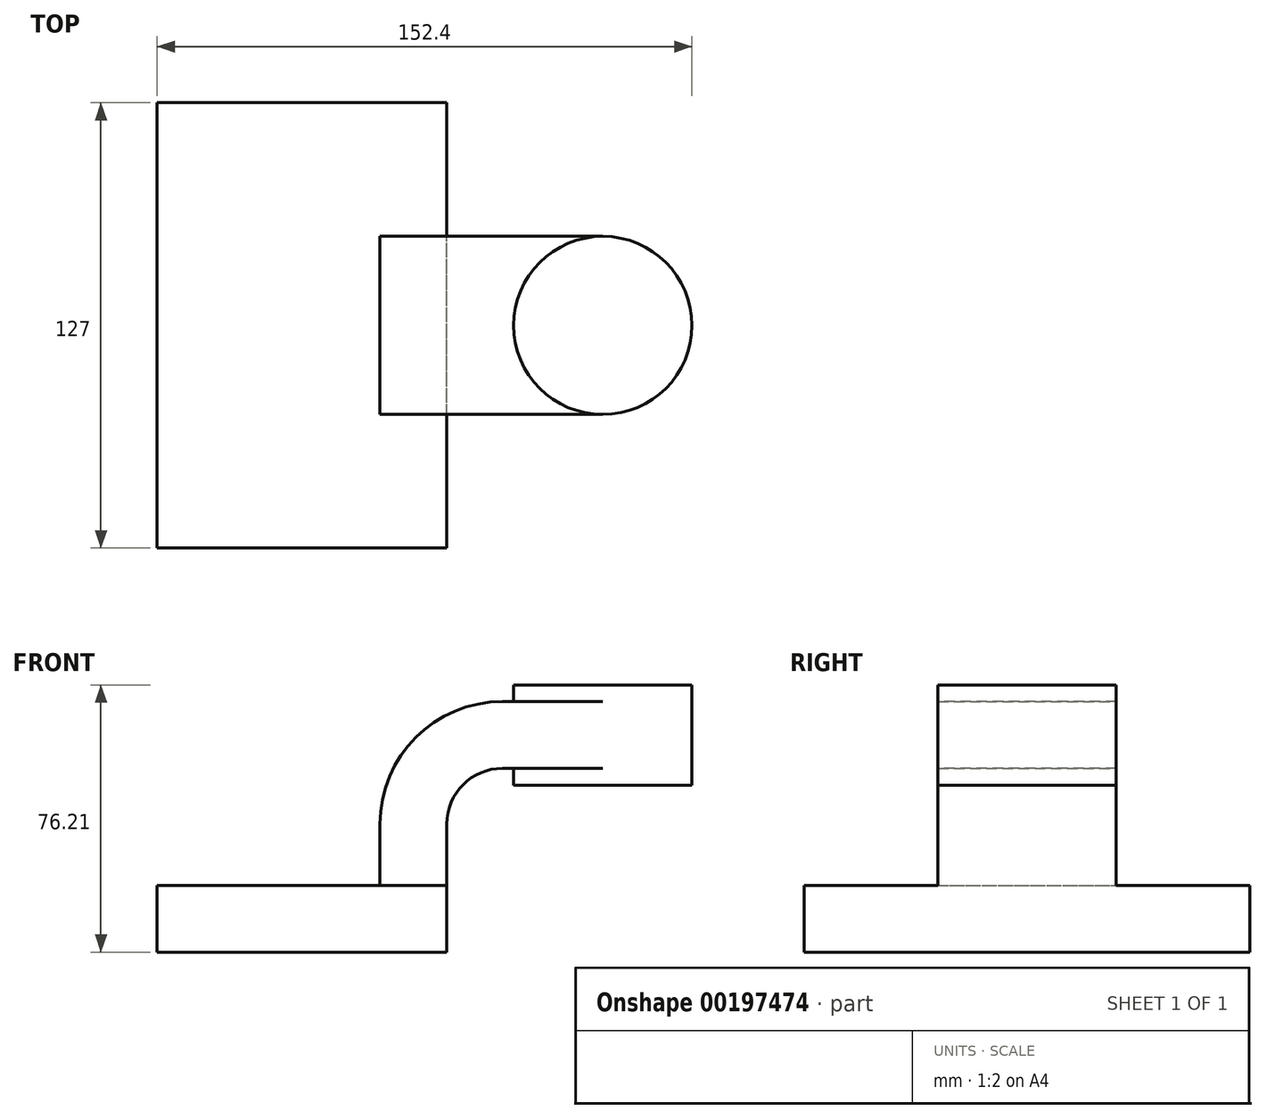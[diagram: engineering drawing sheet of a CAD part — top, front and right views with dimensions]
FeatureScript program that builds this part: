
annotation { "Feature Type Name" : "Feature", "Feature Type Description" : "" }
export const myFeature = defineFeature(function(context is Context, id is Id, definition is map)
    precondition{}
    {
        {
            var Q0;
            Q0=qCreatedBy(makeId("Front.planeOp"),FACE);
            var sketch = newSketch(context, id + "F0", { "sketchPlane" : qUnion([Q0])});
            skLineSegment(sketch, "E0.bottom", {"start": v(-41.27, -9.52) * mm, "end": v(41.28, -9.52) * mm});
            skLineSegment(sketch, "E0.top", {"start": v(-41.28, 9.52) * mm, "end": v(41.27, 9.52) * mm});
            skLineSegment(sketch, "E0.left", {"start": v(-41.27, -9.52) * mm, "end": v(-41.28, 9.52) * mm});
            skLineSegment(sketch, "E0.right", {"start": v(41.28, -9.52) * mm, "end": v(41.27, 9.52) * mm});
            skPoint(sketch, "E0.middle", {"position": v(0, 0) * mm});
            skLineSegment(sketch, "E1.bottom", {"start": v(60.33, 38.1) * mm, "end": v(111.12, 38.1) * mm});
            skLineSegment(sketch, "E1.top", {"start": v(60.32, 66.68) * mm, "end": v(111.12, 66.68) * mm});
            skLineSegment(sketch, "E1.left", {"start": v(60.33, 38.1) * mm, "end": v(60.32, 66.68) * mm});
            skLineSegment(sketch, "E1.right", {"start": v(111.12, 38.1) * mm, "end": v(111.12, 66.68) * mm});
            skPoint(sketch, "E1.middle", {"position": v(85.72, 52.39) * mm});
            skLineSegment(sketch, "E2", {"start": v(41.27, 9.52) * mm, "end": v(41.27, 27) * mm});
            skArc(sketch, "E3", {"start": v(41.27, 27) * mm, "mid": v(45.92, 38.23) * mm, "end": v(57.15, 42.88) * mm});
            skLineSegment(sketch, "E4", {"start": v(57.15, 42.88) * mm, "end": v(85.72, 42.88) * mm});
            skLineSegment(sketch, "E5.0", {"start": v(57.15, 61.93) * mm, "end": v(85.72, 61.93) * mm});
            skArc(sketch, "E5.1", {"start": v(22.23, 27) * mm, "mid": v(32.45, 51.7) * mm, "end": v(57.15, 61.93) * mm});
            skLineSegment(sketch, "E5.2", {"start": v(22.22, 9.52) * mm, "end": v(22.22, 27) * mm});
            skFitSpline(sketch, "E6", {"points": [v(-41.28, 9.53) * mm, v(57.15, 61.93) * mm], "startDerivative": vector(2.22, 88.45) * mm, "endDerivative": vector(124.25, 0) * mm});
            skPoint(sketch, "E7", {"position": v(85.72, 66.68) * mm});
            skLineSegment(sketch, "E8", {"start": v(85.72, 66.68) * mm, "end": v(85.72, 38.1) * mm});
            skSolve(sketch);
        }
        {
            var Q0;
            Q0=makeQuery(id+"F0.imprint","IMPRINT",FACE,{"disambiguationData":[TD([[makeQuery(id+"F0.imprint","IMPRINT",EDGE,{"derivedFrom":sQuery(id+"F0.wireOp",EDGE,"E0.bottom")}),1.0]])]});
            extrude(context, id + "F1", {"entities" : qUnion([Q0]), "endBound" : BoundingType.SYMMETRIC, "depth" : 127 * mm});
        }
        {
            var Q0;
            {var subQ1=sQuery(id+"F0.wireOp",EDGE,"E2");Q0=makeQuery(id+"F0.imprint","IMPRINT",FACE,{"disambiguationData":[TD([[makeQuery(id+"F0.imprint","IMPRINT",EDGE,{"derivedFrom":subQ1}),1.0]])]});}
            var Q1;
            {var subQ0=sQuery(id+"F0.wireOp",EDGE,"E4");var subQ1=sQuery(id+"F0.wireOp",EDGE,"E1.left");var subQ2=makeQuery(id+"F0.imprint","INTERSECT",VERTEX,{"derivedFrom":[subQ1,subQ0]});Q1=makeQuery(id+"F0.imprint","IMPRINT",FACE,{"disambiguationData":[TD([[makeQuery(id+"F0.imprint","IMPRINT",EDGE,{"disambiguationData":[TD([[subQ2,-1.0]])],"derivedFrom":subQ1}),-1.0]])]});}
            extrude(context, id + "F2", {"entities" : qUnion([Q0, Q1]), "operationType" : NewBodyOperationType.ADD, "endBound" : BoundingType.SYMMETRIC, "depth" : 50.8 * mm});
        }
        {
            var Q0;
            Q0=makeQuery(id+"F0.imprint","IMPRINT",FACE,{"disambiguationData":[TD([[makeQuery(id+"F0.imprint","IMPRINT",EDGE,{"derivedFrom":sQuery(id+"F0.wireOp",EDGE,"E5.1")}),1.0]])]});
            extrude(context, id + "F3", {"entities" : qUnion([Q0]), "operationType" : NewBodyOperationType.ADD, "endBound" : BoundingType.SYMMETRIC, "depth" : 15.88 * mm});
        }
        {
            var Q0;
            {var subQ0=sQuery(id+"F0.wireOp",EDGE,"E1.right");Q0=makeQuery(id+"F0.imprint","IMPRINT",FACE,{"disambiguationData":[TD([[makeQuery(id+"F0.imprint","IMPRINT",EDGE,{"derivedFrom":subQ0}),1.0]])]});}
            var Q1;
            Q1=sQuery(id+"F0.wireOp",EDGE,"E8");
            revolve(context, id + "F4", {"operationType" : NewBodyOperationType.ADD, "entities" : qUnion([Q0]), "axis" : qUnion([Q1]), "revolveType" : RevolveType.FULL});
        }
    });
